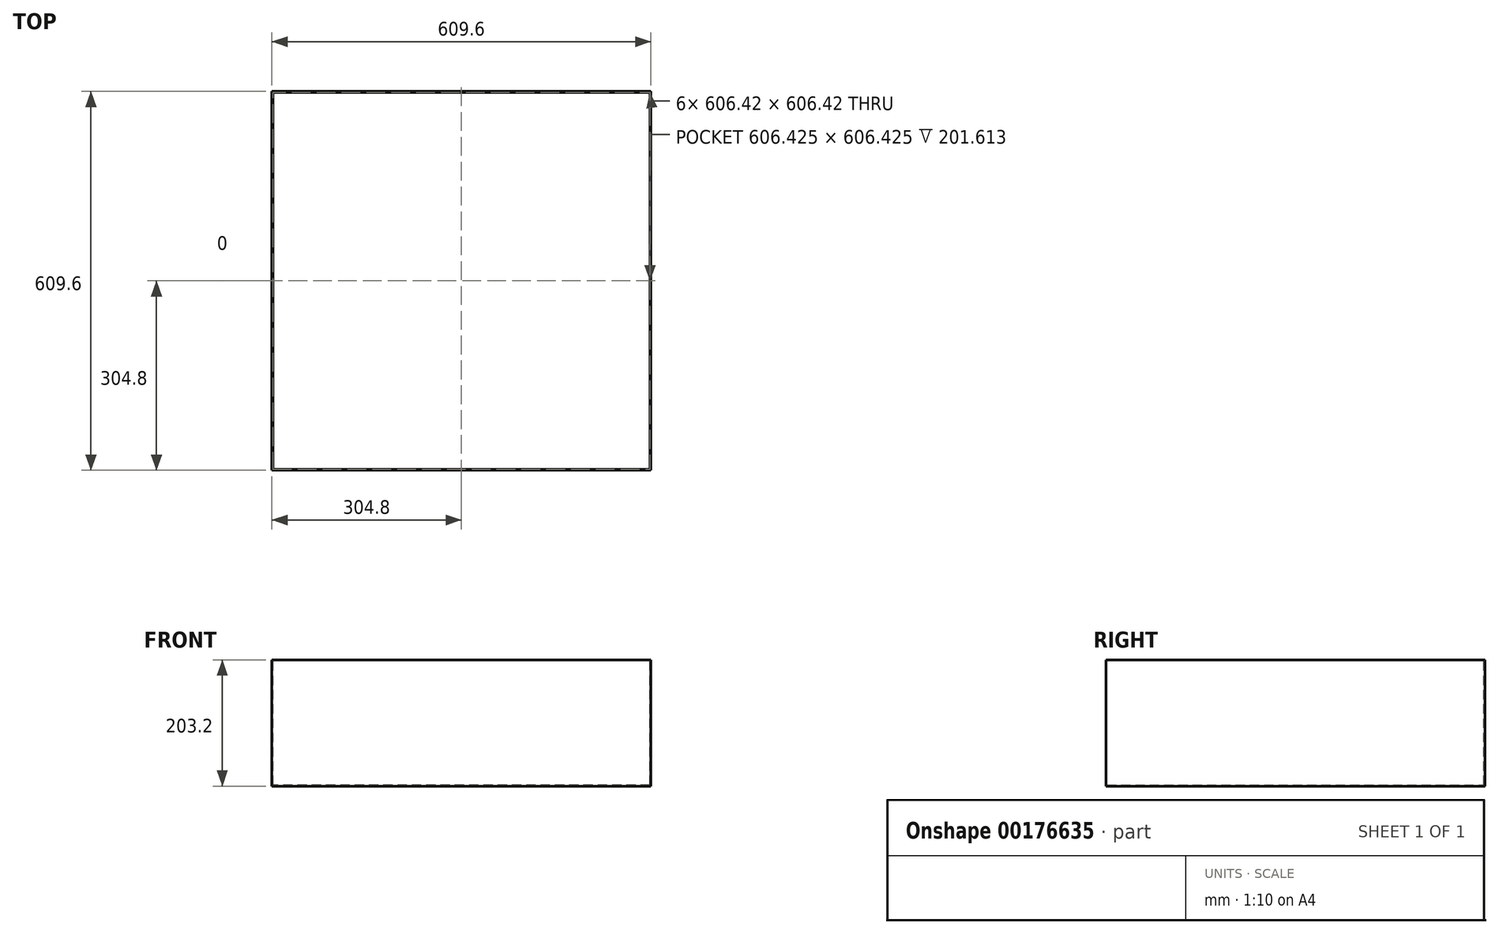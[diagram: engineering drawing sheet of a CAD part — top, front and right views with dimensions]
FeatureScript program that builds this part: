
annotation { "Feature Type Name" : "Feature", "Feature Type Description" : "" }
export const myFeature = defineFeature(function(context is Context, id is Id, definition is map)
    precondition{}
    {
        {
            var Q0;
            Q0=qCreatedBy(makeId("Top.planeOp"),FACE);
            var sketch = newSketch(context, id + "F0", { "sketchPlane" : qUnion([Q0])});
            skLineSegment(sketch, "E0.bottom", {"start": v(292.1, -292.1) * mm, "end": v(-292.1, -292.1) * mm});
            skLineSegment(sketch, "E0.top", {"start": v(292.1, 292.1) * mm, "end": v(-292.1, 292.1) * mm});
            skLineSegment(sketch, "E0.left", {"start": v(292.1, -292.1) * mm, "end": v(292.1, 292.1) * mm});
            skLineSegment(sketch, "E0.right", {"start": v(-292.1, -292.1) * mm, "end": v(-292.1, 292.1) * mm});
            skPoint(sketch, "E0.middle", {"position": v(0, 0) * mm});
            skSolve(sketch);
        }
        {
            var Q0;
            Q0=makeQuery(id+"F0.imprint","IMPRINT",FACE,{"disambiguationData":[TD([[makeQuery(id+"F0.imprint","IMPRINT",EDGE,{"derivedFrom":sQuery(id+"F0.wireOp",EDGE,"E0.bottom")}),-1.0]])]});
            extrude(context, id + "F1", {"entities" : qUnion([Q0]), "depth" : 19.05 * mm});
        }
        {
            var Q0;
            Q0=makeQuery(id+"F1.opExtrude","CAP_FACE",FACE,{"disambiguationData":[OSD([sQuery(id+"F0.wireOp",EDGE,"E0.bottom"),sQuery(id+"F0.wireOp",EDGE,"E0.top"),sQuery(id+"F0.wireOp",EDGE,"E0.left"),sQuery(id+"F0.wireOp",EDGE,"E0.right")])],"isStart":true});
            cPlane(context, id + "F2", {"entities" : qUnion([Q0]), "cplaneType" : CPlaneType.OFFSET, "offset" : 1.59 * mm, "width" : 152.4 * mm, "height" : 152.4 * mm});
        }
        {
            var Q0;
            Q0=qCreatedBy(id+"F2.planeOp",FACE);
            var sketch = newSketch(context, id + "F3", { "sketchPlane" : qUnion([Q0])});
            skLineSegment(sketch, "E1.bottom", {"start": v(-304.8, -304.8) * mm, "end": v(304.8, -304.8) * mm});
            skLineSegment(sketch, "E1.top", {"start": v(-304.8, 304.8) * mm, "end": v(304.8, 304.8) * mm});
            skLineSegment(sketch, "E1.left", {"start": v(-304.8, -304.8) * mm, "end": v(-304.8, 304.8) * mm});
            skLineSegment(sketch, "E1.right", {"start": v(304.8, -304.8) * mm, "end": v(304.8, 304.8) * mm});
            skPoint(sketch, "E1.middle", {"position": v(0, 0) * mm});
            skSolve(sketch);
        }
        {
            var Q0;
            Q0 = qSketchRegion(id + "F3", true);
            extrude(context, id + "F4", {"entities" : qUnion([Q0]), "oppositeDirection" : true, "depth" : 203.2 * mm});
        }
        {
            var Q0;
            Q0=makeQuery(id+"F4.opExtrude","CAP_FACE",FACE,{"disambiguationData":[OSD([sQuery(id+"F3.wireOp",EDGE,"E1.bottom"),sQuery(id+"F3.wireOp",EDGE,"E1.top"),sQuery(id+"F3.wireOp",EDGE,"E1.left"),sQuery(id+"F3.wireOp",EDGE,"E1.right")])],"isStart":false});
            var sketch = newSketch(context, id + "F5", { "sketchPlane" : qUnion([Q0])});
            skLineSegment(sketch, "E2.0", {"start": v(-303.21, 303.21) * mm, "end": v(-303.21, -303.21) * mm});
            skLineSegment(sketch, "E2.1", {"start": v(-303.21, 303.21) * mm, "end": v(303.21, 303.21) * mm});
            skLineSegment(sketch, "E2.2", {"start": v(303.21, 303.21) * mm, "end": v(303.21, -303.21) * mm});
            skLineSegment(sketch, "E2.3", {"start": v(-303.21, -303.21) * mm, "end": v(303.21, -303.21) * mm});
            skSolve(sketch);
        }
        {
            var Q0;
            Q0 = qSketchRegion(id + "F5", true);
            var Q1;
            Q1=qCreatedBy(makeId("Top.planeOp"),FACE);
            extrude(context, id + "F6", {"entities" : qUnion([Q0]), "operationType" : NewBodyOperationType.REMOVE, "endBound" : BoundingType.UP_TO_SURFACE, "oppositeDirection" : true, "endBoundEntityFace" : qUnion([Q1]), "depth" : 25.4 * mm});
        }
    });
